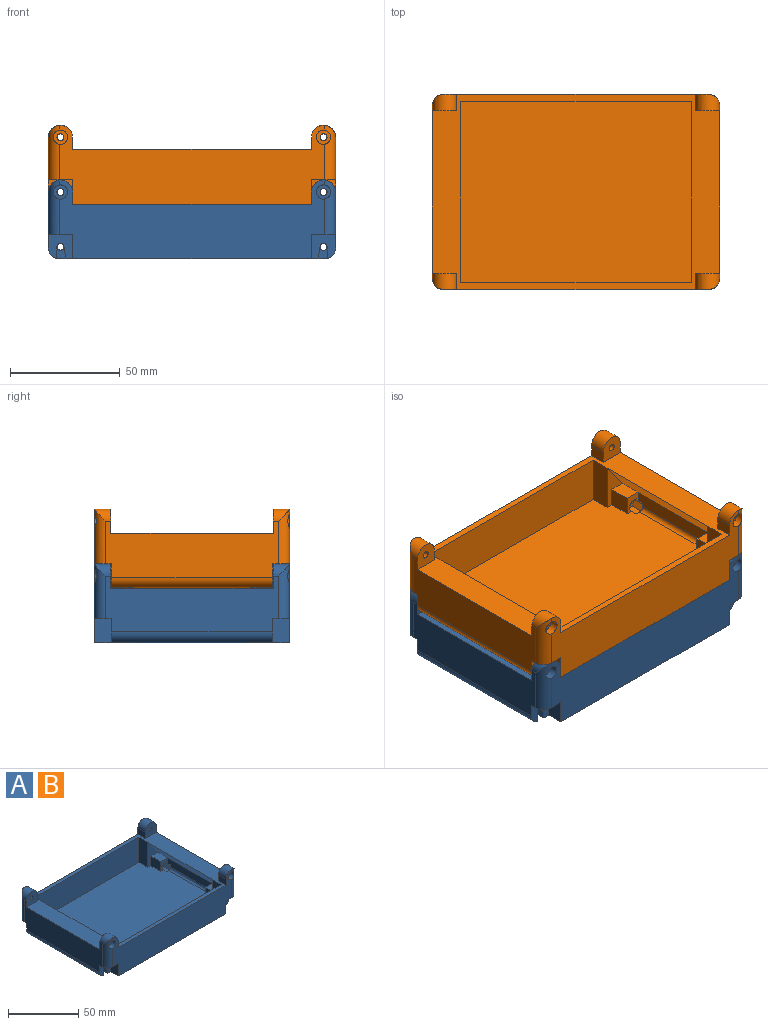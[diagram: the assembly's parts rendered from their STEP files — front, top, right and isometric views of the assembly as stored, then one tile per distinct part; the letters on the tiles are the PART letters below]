
ASSEMBLY  parts=2 mates=1
PART A: 125 faces, bbox 131x89x36 mm
  f0: cylinder r=1.6mm len=11.3mm, axis (0,-1,0), area 60.7mm2, adj f2,f120,f122,f123,f124
  f1: cylinder r=5mm len=73.6mm, axis (0,1,0), area 555.9mm2, adj f2,f8,f32,f33,f108,f110,f122,f124
  f2: plane 11.2x11mm, normal (0,-1,0), area 93.6mm2, adj f0,f1,f32,f33,f45,f46,f122,f123
  f3: plane 121x83mm, normal (0,0,1), area 9527.3mm2, adj f5,f19,f28,f29,f30,f31,f34,f35
  f4: plane 45x6.54mm, normal (-1,0,0), area 283.4mm2, adj f5,f34,f60,f64,f100,f107,f114,f121
  f5: plane 8.54x7mm, normal (0,1,0), area 34mm2, adj f3,f4,f58,f59,f114,f117,f118,f119
  f6: plane 121x36mm, normal (0,-1,0), area 2968mm2, adj f7,f14,f25,f26,f33,f40,f45,f46
  f7: cylinder r=5mm len=24.98mm, axis (0,0,-1), area 165.9mm2, adj f6,f32,f46,f65,f113
  f8: plane 11.2x11mm, normal (0,1,0), area 93.6mm2, adj f1,f9,f32,f33,f47,f48,f108,f109
  f9: cylinder r=1.6mm len=11.3mm, axis (0,1,0), area 60.7mm2, adj f8,f106,f108,f109,f110
  f10: plane 121x36mm, normal (0,1,0), area 2968mm2, adj f11,f20,f33,f36,f39,f40,f47,f48
  f11: cylinder r=5mm len=24.98mm, axis (0,0,-1), area 165.9mm2, adj f10,f32,f48,f68,f99
  f12: plane 11.2x11mm, normal (0,-1,0), area 93.6mm2, adj f13,f16,f27,f33,f49,f50,f94,f95
  f13: cylinder r=1.6mm len=11.3mm, axis (0,-1,0), area 60.7mm2, adj f12,f93,f94,f95,f96
  f14: cylinder r=5mm len=24.98mm, axis (0,0,-1), area 165.9mm2, adj f6,f27,f50,f67,f85
  f15: cylinder r=1.6mm len=11.3mm, axis (0,1,0), area 60.7mm2, adj f17,f79,f80,f81,f82
  f16: cylinder r=5mm len=73.6mm, axis (0,-1,0), area 555.9mm2, adj f12,f17,f27,f33,f80,f82,f94,f96
  f17: plane 11.2x11mm, normal (0,1,0), area 93.6mm2, adj f15,f16,f27,f33,f51,f52,f80,f81
  f18: plane 45x6.54mm, normal (1,0,0), area 283.4mm2, adj f19,f38,f53,f63,f72,f73,f86,f87
  f19: plane 8.54x7mm, normal (0,-1,0), area 34mm2, adj f3,f18,f56,f57,f73,f76,f77,f78
  f20: cylinder r=5mm len=24.98mm, axis (0,0,-1), area 165.9mm2, adj f10,f27,f52,f66,f71
  f21: plane 11x11mm, normal (0,1,0), area 100mm2, adj f25,f32,f40,f65,f111
  f22: plane 11x11mm, normal (0,-1,0), area 100mm2, adj f32,f36,f40,f68,f97
  f23: plane 11x11mm, normal (0,1,0), area 100mm2, adj f26,f27,f40,f67,f83
  f24: plane 11x11mm, normal (0,-1,0), area 100mm2, adj f27,f39,f40,f66,f69
  f25: plane 7.5x5.5mm, normal (-1,0,0), area 41.2mm2, adj f6,f21,f40,f65
  f26: plane 7.5x5.5mm, normal (1,0,0), area 41.2mm2, adj f6,f23,f40,f67
  f27: plane 79x25.5mm, normal (-1,0,0), area 1575.1mm2, adj f12,f14,f16,f17,f20,f23,f24,f40
  f28: plane 22x10mm, normal (0,1,0), area 92.9mm2, adj f3,f44,f58,f59,f64
  f29: plane 22x10mm, normal (0,1,0), area 92.9mm2, adj f3,f42,f54,f55,f63
  f30: plane 22x10mm, normal (0,-1,0), area 92.9mm2, adj f3,f43,f61,f62,f64
  f31: plane 22x10mm, normal (0,-1,0), area 92.9mm2, adj f3,f41,f56,f57,f63
  f32: plane 79x25.5mm, normal (1,0,0), area 1575.1mm2, adj f1,f2,f7,f8,f11,f21,f22,f40
  f33: plane 121x89mm, normal (0,0,-1), area 10456.2mm2, adj f1,f2,f6,f8,f10,f12,f16,f17
  f34: cylinder r=2mm len=39mm, axis (0,1,0), area 122.5mm2, adj f3,f4,f107,f121
  f35: plane 105x22mm, normal (0,1,0), area 2310mm2, adj f3,f40,f42,f44
  f36: plane 7.5x5.5mm, normal (-1,0,0), area 41.2mm2, adj f10,f22,f40,f68
  f37: plane 105x22mm, normal (0,-1,0), area 2310mm2, adj f3,f40,f41,f43
  f38: cylinder r=2mm len=39mm, axis (0,-1,0), area 122.5mm2, adj f3,f18,f72,f86
  f39: plane 7.5x5.5mm, normal (1,0,0), area 41.2mm2, adj f10,f24,f40,f66
  f40: plane 131x89mm, normal (0,0,1), area 2614mm2, adj f6,f10,f21,f22,f23,f24,f25,f26
  f41: plane 22x9mm, normal (1,0,0), area 198mm2, adj f3,f31,f37,f40
  f42: plane 22x9mm, normal (1,0,0), area 198mm2, adj f3,f29,f35,f40
  f43: plane 22x9mm, normal (-1,0,0), area 198mm2, adj f3,f30,f37,f40
  f44: plane 22x9mm, normal (-1,0,0), area 198mm2, adj f3,f28,f35,f40
  f45: plane 11x7.7mm, normal (1,0,0), area 84.7mm2, adj f2,f6,f33,f46
  f46: plane 11.2x7.7mm, normal (0,0,-1), area 80.9mm2, adj f2,f6,f7,f32,f45
  f47: plane 11x7.7mm, normal (1,0,0), area 84.7mm2, adj f8,f10,f33,f48
  f48: plane 11.2x7.7mm, normal (0,0,-1), area 80.9mm2, adj f8,f10,f11,f32,f47
  f49: plane 11x7.7mm, normal (-1,0,0), area 84.7mm2, adj f6,f12,f33,f50
  f50: plane 11.2x7.7mm, normal (0,0,-1), area 80.9mm2, adj f6,f12,f14,f27,f49
  f51: plane 11x7.7mm, normal (-1,0,0), area 84.7mm2, adj f10,f17,f33,f52
  f52: plane 11.2x7.7mm, normal (0,0,-1), area 80.9mm2, adj f10,f17,f20,f27,f51
  f53: plane 8.54x7mm, normal (0,1,0), area 34mm2, adj f3,f18,f54,f55,f87,f88,f89,f90
  f54: plane 10x7mm, normal (0,0,1), area 70mm2, adj f29,f53,f55,f63
  f55: plane 10x8.54mm, normal (1,0,0), area 85.4mm2, adj f3,f29,f53,f54
  f56: plane 10x8.54mm, normal (1,0,0), area 85.4mm2, adj f3,f19,f31,f57
  f57: plane 10x7mm, normal (0,0,1), area 70mm2, adj f19,f31,f56,f63
  f58: plane 10x8.54mm, normal (-1,0,0), area 85.4mm2, adj f3,f5,f28,f59
  f59: plane 10x7mm, normal (0,0,1), area 70mm2, adj f5,f28,f58,f64
  f60: plane 8.54x7mm, normal (0,-1,0), area 34mm2, adj f3,f4,f61,f62,f100,f101,f102,f103
  f61: plane 10x7mm, normal (0,0,1), area 70mm2, adj f30,f60,f62,f64
  f62: plane 10x8.54mm, normal (-1,0,0), area 85.4mm2, adj f3,f30,f60,f61
  f63: plane 65x13.46mm, normal (0.8,0,-0.6), area 1090.1mm2, adj f18,f29,f31,f40,f54,f57
  f64: plane 65x13.46mm, normal (-0.8,0,-0.6), area 1090.1mm2, adj f4,f28,f30,f40,f59,f61
  f65: cylinder r=5.5mm len=11mm, axis (0,1,0), area 114.7mm2, adj f6,f7,f21,f25,f32
  f66: cylinder r=5.5mm len=11mm, axis (0,1,0), area 114.7mm2, adj f10,f20,f24,f27,f39
  f67: cylinder r=5.5mm len=11mm, axis (0,1,0), area 114.7mm2, adj f6,f14,f23,f26,f27
  f68: cylinder r=5.5mm len=11mm, axis (0,1,0), area 114.7mm2, adj f10,f11,f22,f32,f36
  f69: cylinder r=1.6mm len=3.68mm, axis (0,1,0), area 37mm2, adj f24,f70
  f70: plane 6.5x6.5mm, normal (0,1,0), area 25.1mm2, adj f69,f71
  f71: cylinder r=3.25mm len=6.5mm, axis (0,1,0), area 74.3mm2, adj f10,f20,f70
  f72: plane 5.06x4.11mm, normal (0,1,0), area 2.5mm2, adj f3,f18,f38,f73,f74,f75,f76
  f73: plane 6x2.81mm, normal (0.87,0,-0.5), area 14.3mm2, adj f18,f19,f72,f74,f78,f79
  f74: plane 6x2.81mm, normal (0.87,0,0.5), area 19.5mm2, adj f72,f73,f75,f79
  f75: plane 6x3.25mm, normal (0,0,1), area 19.5mm2, adj f72,f74,f76,f79
  f76: plane 6x2.81mm, normal (-0.87,0,0.5), area 10.8mm2, adj f3,f19,f72,f75,f77,f79
  f77: plane 3x2.81mm, normal (-0.87,0,-0.5), area 9.8mm2, adj f19,f76,f78,f79
  f78: plane 3.25x3mm, normal (0,0,-1), area 9.7mm2, adj f19,f73,f77,f79
  f79: plane 6.5x5.63mm, normal (0,-1,0), area 19.4mm2, adj f15,f73,f74,f75,f76,f77,f78
  f80: plane 10x5.38mm, normal (1,0,0), area 53.8mm2, adj f15,f16,f17,f82
  f81: plane 10x5.77mm, normal (-0.99,0,-0.17), area 58.5mm2, adj f15,f17,f33,f82
  f82: plane 5.76x4.15mm, normal (0,1,0), area 16.2mm2, adj f15,f16,f33,f80,f81
  f83: cylinder r=1.6mm len=3.68mm, axis (0,-1,0), area 37mm2, adj f23,f84
  f84: plane 6.5x6.5mm, normal (0,-1,0), area 25.1mm2, adj f83,f85
  f85: cylinder r=3.25mm len=6.5mm, axis (0,-1,0), area 74.3mm2, adj f6,f14,f84
  f86: plane 5.06x4.11mm, normal (0,-1,0), area 2.5mm2, adj f3,f18,f38,f87,f90,f91,f92
  f87: plane 6x2.81mm, normal (0.87,0,-0.5), area 14.3mm2, adj f18,f53,f86,f88,f92,f93
  f88: plane 3.25x3mm, normal (0,0,-1), area 9.7mm2, adj f53,f87,f89,f93
  f89: plane 3x2.81mm, normal (-0.87,0,-0.5), area 9.8mm2, adj f53,f88,f90,f93
  f90: plane 6x2.81mm, normal (-0.87,0,0.5), area 10.8mm2, adj f3,f53,f86,f89,f91,f93
  f91: plane 6x3.25mm, normal (0,0,1), area 19.5mm2, adj f86,f90,f92,f93
  f92: plane 6x2.81mm, normal (0.87,0,0.5), area 19.5mm2, adj f86,f87,f91,f93
  f93: plane 6.5x5.63mm, normal (0,1,0), area 19.4mm2, adj f13,f87,f88,f89,f90,f91,f92
  f94: plane 10x5.38mm, normal (1,0,0), area 53.8mm2, adj f12,f13,f16,f96
  f95: plane 10x5.77mm, normal (-0.99,0,-0.17), area 58.5mm2, adj f12,f13,f33,f96
  f96: plane 5.76x4.15mm, normal (0,-1,0), area 16.2mm2, adj f13,f16,f33,f94,f95
  f97: cylinder r=1.6mm len=3.68mm, axis (0,1,0), area 37mm2, adj f22,f98
  f98: plane 6.5x6.5mm, normal (0,1,0), area 25.1mm2, adj f97,f99
  f99: cylinder r=3.25mm len=6.5mm, axis (0,1,0), area 74.3mm2, adj f10,f11,f98
  f100: plane 6x2.81mm, normal (-0.87,0,-0.5), area 14.3mm2, adj f4,f60,f101,f105,f106,f107
  f101: plane 3.25x3mm, normal (0,0,-1), area 9.7mm2, adj f60,f100,f102,f106
  f102: plane 3x2.81mm, normal (0.87,0,-0.5), area 9.8mm2, adj f60,f101,f103,f106
  f103: plane 6x2.81mm, normal (0.87,0,0.5), area 10.8mm2, adj f3,f60,f102,f104,f106,f107
  f104: plane 6x3.25mm, normal (0,0,1), area 19.5mm2, adj f103,f105,f106,f107
  f105: plane 6x2.81mm, normal (-0.87,0,0.5), area 19.5mm2, adj f100,f104,f106,f107
  f106: plane 6.5x5.63mm, normal (0,-1,0), area 19.4mm2, adj f9,f100,f101,f102,f103,f104,f105
  f107: plane 5.06x4.11mm, normal (0,1,0), area 2.5mm2, adj f3,f4,f34,f100,f103,f104,f105
  f108: plane 10x5.38mm, normal (-1,0,0), area 53.8mm2, adj f1,f8,f9,f110
  f109: plane 10x5.77mm, normal (0.99,0,-0.17), area 58.5mm2, adj f8,f9,f33,f110
  f110: plane 5.76x4.15mm, normal (0,1,0), area 16.2mm2, adj f1,f9,f33,f108,f109
  f111: cylinder r=1.6mm len=3.68mm, axis (0,-1,0), area 37mm2, adj f21,f112
  f112: plane 6.5x6.5mm, normal (0,-1,0), area 25.1mm2, adj f111,f113
  f113: cylinder r=3.25mm len=6.5mm, axis (0,-1,0), area 74.3mm2, adj f6,f7,f112
  f114: plane 6x2.81mm, normal (-0.87,0,-0.5), area 14.3mm2, adj f4,f5,f115,f119,f120,f121
  f115: plane 6x2.81mm, normal (-0.87,0,0.5), area 19.5mm2, adj f114,f116,f120,f121
  f116: plane 6x3.25mm, normal (0,0,1), area 19.5mm2, adj f115,f117,f120,f121
  f117: plane 6x2.81mm, normal (0.87,0,0.5), area 10.8mm2, adj f3,f5,f116,f118,f120,f121
  f118: plane 3x2.81mm, normal (0.87,0,-0.5), area 9.8mm2, adj f5,f117,f119,f120
  f119: plane 3.25x3mm, normal (0,0,-1), area 9.7mm2, adj f5,f114,f118,f120
  f120: plane 6.5x5.63mm, normal (0,1,0), area 19.4mm2, adj f0,f114,f115,f116,f117,f118,f119
  f121: plane 5.06x4.11mm, normal (0,-1,0), area 2.5mm2, adj f3,f4,f34,f114,f115,f116,f117
  f122: plane 10x5.38mm, normal (-1,0,0), area 53.8mm2, adj f0,f1,f2,f124
  f123: plane 10x5.77mm, normal (0.99,0,-0.17), area 58.5mm2, adj f0,f2,f33,f124
  f124: plane 5.76x4.15mm, normal (0,-1,0), area 16.2mm2, adj f0,f1,f33,f122,f123
PART B: same geometry as A
PLACE A t=(-7.7,9.82,-17.14)mm
PLACE B t=(-7.7,9.77,7.86)mm
MATE fastened B.f15 <-> A.f66  axis (0,1,0) through (-57.7,40.07,13.36)mm
